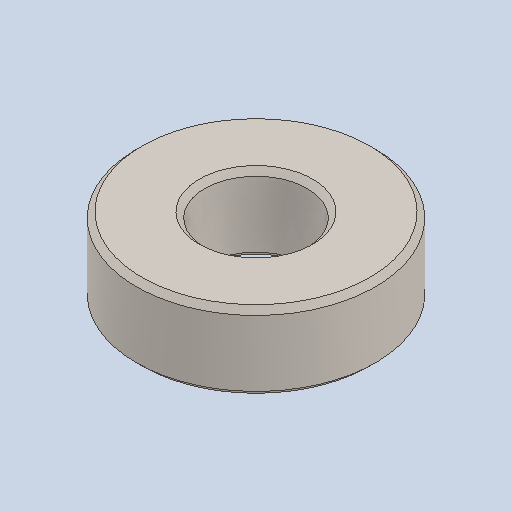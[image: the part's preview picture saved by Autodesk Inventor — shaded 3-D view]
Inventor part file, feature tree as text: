
AUTODESK INVENTOR PART (.ipt)
format: ipt  version: 2023.2 (Build 272271000, 271)  size: 105,472 bytes
history: native  units: in
note: dims shown in document units (in); Inventor stores cm internally (conversion verified against a paired STEP export)
features: chamfer x1
ambient origin geometry x8: Origin, YZ Plane, XZ Plane, XY Plane, X Axis, Y Axis, Z Axis, Center Point
bodies: Solid1 (feature_tree)
feature tree (1):
  chamfer  "Chamfer1"  [1 undecoded]
note: 1 required parameter value undecoded (feature->parameter linkage not recoverable at this tier; creation-order binding heuristic only, values carry confidence <= 0.55)
